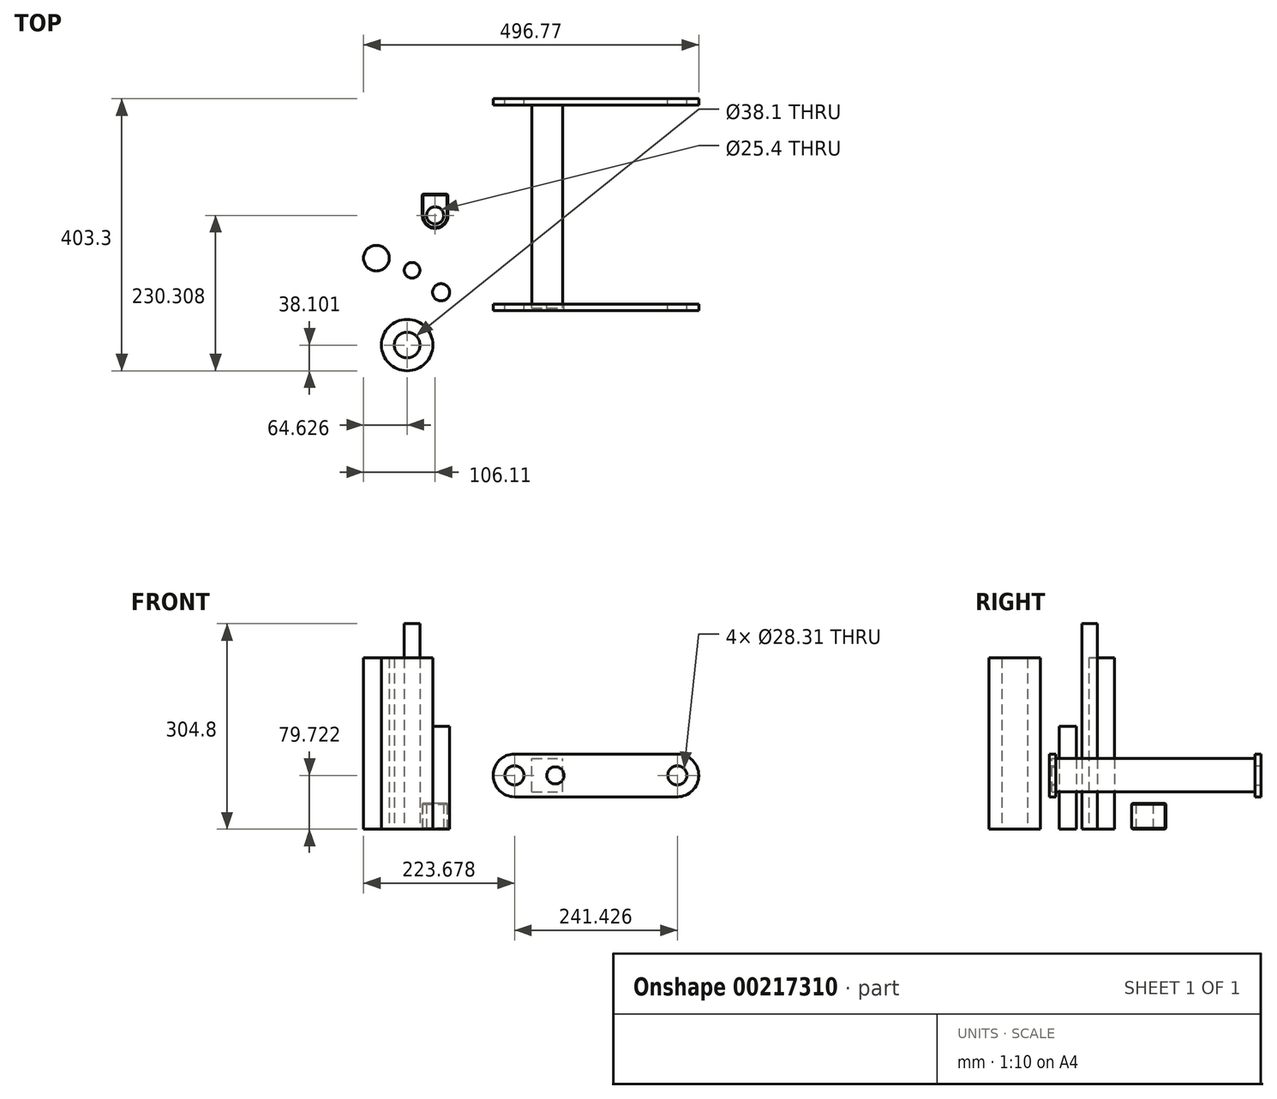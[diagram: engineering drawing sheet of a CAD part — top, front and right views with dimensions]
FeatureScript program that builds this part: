
annotation { "Feature Type Name" : "Feature", "Feature Type Description" : "" }
export const myFeature = defineFeature(function(context is Context, id is Id, definition is map)
    precondition{}
    {
        {
            var Q0;
            Q0=qCreatedBy(makeId("Front.planeOp"),FACE);
            var sketch = newSketch(context, id + "F0", { "sketchPlane" : qUnion([Q0])});
            skLineSegment(sketch, "E0.bottom", {"start": v(-15.65, 47.97) * mm, "end": v(225.65, 47.97) * mm});
            skLineSegment(sketch, "E0.top", {"start": v(-15.65, 111.47) * mm, "end": v(225.65, 111.47) * mm});
            skLineSegment(sketch, "E0.left", {"start": v(-47.4, 79.72) * mm, "end": v(-47.4, 79.72) * mm});
            skLineSegment(sketch, "E0.right", {"start": v(257.4, 79.72) * mm, "end": v(257.4, 79.72) * mm});
            skPoint(sketch, "E1.visualSharp", {"position": v(-47.4, 111.47) * mm});
            skArc(sketch, "E1.filletArc", {"start": v(-15.65, 111.47) * mm, "mid": v(-38.1, 102.17) * mm, "end": v(-47.4, 79.72) * mm});
            skPoint(sketch, "E2.visualSharp", {"position": v(-47.4, 47.97) * mm});
            skArc(sketch, "E2.filletArc", {"start": v(-47.4, 79.72) * mm, "mid": v(-38.1, 57.27) * mm, "end": v(-15.65, 47.97) * mm});
            skPoint(sketch, "E3.visualSharp", {"position": v(257.4, 47.97) * mm});
            skArc(sketch, "E3.filletArc", {"start": v(225.65, 47.97) * mm, "mid": v(248.1, 57.27) * mm, "end": v(257.4, 79.72) * mm});
            skPoint(sketch, "E4.visualSharp", {"position": v(257.4, 111.47) * mm});
            skArc(sketch, "E4.filletArc", {"start": v(257.4, 79.72) * mm, "mid": v(248.1, 102.17) * mm, "end": v(225.65, 111.47) * mm});
            skSolve(sketch);
        }
        {
            var Q0;
            Q0=makeQuery(id+"F0.imprint","IMPRINT",FACE,{"disambiguationData":[TD([[makeQuery(id+"F0.imprint","IMPRINT",EDGE,{"derivedFrom":sQuery(id+"F0.wireOp",EDGE,"E0.bottom")}),1.0]])]});
            var sketch = newSketch(context, id + "F1", { "sketchPlane" : qUnion([Q0])});
            skCircle(sketch, "E5", {"center": v(225.73, 79.72) * mm, "radius": 14.15 * mm});
            skCircle(sketch, "E6", {"center": v(-15.7, 79.72) * mm, "radius": 14.15 * mm});
            skSolve(sketch);
        }
        {
            var Q0;
            Q0=makeQuery(id+"F1.imprint","IMPRINT",FACE,{"disambiguationData":[TD([[makeQuery(id+"F1.imprint","IMPRINT",EDGE,{"derivedFrom":sQuery(id+"F1.wireOp",EDGE,"E5")}),-1.0]])]});
            var sketch = newSketch(context, id + "F2", { "sketchPlane" : qUnion([Q0])});
            skCircle(sketch, "E7", {"center": v(44.9, 79.72) * mm, "radius": 12.7 * mm});
            skSolve(sketch);
        }
        {
            var Q0;
            Q0=makeQuery(id+"F1.imprint","IMPRINT",FACE,{"disambiguationData":[TD([[makeQuery(id+"F1.imprint","IMPRINT",EDGE,{"derivedFrom":sQuery(id+"F1.wireOp",EDGE,"E5")}),-1.0]])]});
            var Q1;
            Q1 = qSketchRegion(id + "F2", true);
            extrude(context, id + "F3", {"entities" : qUnion([Q0, Q1]), "depth" : 9.52 * mm});
        }
        {
            var Q0;
            Q0=makeQuery(id+"F3.opExtrude","SWEPT_BODY",BODY,{"disambiguationData":[OSD([sQuery(id+"F0.wireOp",EDGE,"E0.bottom"),sQuery(id+"F0.wireOp",EDGE,"E0.top"),sQuery(id+"F0.wireOp",EDGE,"E1.filletArc"),sQuery(id+"F0.wireOp",EDGE,"E2.filletArc"),sQuery(id+"F0.wireOp",EDGE,"E3.filletArc"),sQuery(id+"F0.wireOp",EDGE,"E4.filletArc"),sQuery(id+"F1.wireOp",EDGE,"E5"),sQuery(id+"F1.wireOp",EDGE,"E6")])]});
            transform(context, id + "F4", {"entities" : qUnion([Q0]), "transformType" : TransformType.TRANSLATION_3D, "dx" : 0 * mm, "dy" : 304.8 * mm, "dz" : 0 * mm, "makeCopy" : true});
        }
        {
            var Q0;
            Q0=sQuery(id+"F1.wireOp",EDGE,"E6");
            extrude(context, id + "F5", {"bodyType" : ToolBodyType.SURFACE, "surfaceEntities" : qUnion([Q0]), "oppositeDirection" : true, "depth" : 335.28 * mm, "hasSecondDirection" : true, "secondDirectionOppositeDirection" : false, "secondDirectionDepth" : 48.26 * mm});
        }
        {
            var Q0;
            Q0=makeQuery(id+"F5.opExtrude","SWEPT_BODY",BODY,{"disambiguationData":[OSD([sQuery(id+"F1.wireOp",EDGE,"E6")])]});
            transform(context, id + "F6", {"entities" : qUnion([Q0]), "transformType" : TransformType.TRANSLATION_3D, "dx" : 241.3 * mm, "dy" : 0 * mm, "dz" : 0 * mm, "makeCopy" : true});
        }
        {
            var Q0;
            Q0=makeQuery(id+"F4.opPattern","COPY",FACE,{"derivedFrom":makeQuery(id+"F3.opExtrude","CAP_FACE",FACE,{"disambiguationData":[OSD([sQuery(id+"F0.wireOp",EDGE,"E0.bottom"),sQuery(id+"F0.wireOp",EDGE,"E0.top"),sQuery(id+"F0.wireOp",EDGE,"E1.filletArc"),sQuery(id+"F0.wireOp",EDGE,"E2.filletArc"),sQuery(id+"F0.wireOp",EDGE,"E3.filletArc"),sQuery(id+"F0.wireOp",EDGE,"E4.filletArc"),sQuery(id+"F1.wireOp",EDGE,"E5"),sQuery(id+"F1.wireOp",EDGE,"E6")])],"isStart":false}),"instanceName":"1"});
            var sketch = newSketch(context, id + "F7", { "sketchPlane" : qUnion([Q0])});
            skLineSegment(sketch, "E8.bottom", {"start": v(10.28, 55.34) * mm, "end": v(56, 55.34) * mm});
            skLineSegment(sketch, "E8.top", {"start": v(10.28, 104.82) * mm, "end": v(56, 104.82) * mm});
            skLineSegment(sketch, "E8.left", {"start": v(10.28, 55.34) * mm, "end": v(10.28, 104.82) * mm});
            skLineSegment(sketch, "E8.right", {"start": v(56, 55.34) * mm, "end": v(56, 104.82) * mm});
            skSolve(sketch);
        }
        {
            var Q0;
            Q0=makeQuery(id+"F7.imprint","IMPRINT",FACE,{"disambiguationData":[TD([[makeQuery(id+"F7.imprint","IMPRINT",EDGE,{"derivedFrom":sQuery(id+"F7.wireOp",EDGE,"E8.bottom")}),1.0]])]});
            extrude(context, id + "F8", {"entities" : qUnion([Q0]), "depth" : 301 * mm});
        }
        {
            var Q0;
            Q0=qCreatedBy(makeId("Top.planeOp"),FACE);
            var sketch = newSketch(context, id + "F9", { "sketchPlane" : qUnion([Q0])});
            skCircle(sketch, "E9", {"center": v(-167.47, 50.47) * mm, "radius": 11.62 * mm});
            skSolve(sketch);
        }
        {
            var Q0;
            Q0=makeQuery(id+"F9.imprint","IMPRINT",FACE,{"disambiguationData":[TD([[makeQuery(id+"F9.imprint","IMPRINT",EDGE,{"derivedFrom":sQuery(id+"F9.wireOp",EDGE,"E9")}),1.0]])]});
            extrude(context, id + "F10", {"entities" : qUnion([Q0]), "depth" : 304.8 * mm});
        }
        {
            var Q0;
            Q0=qCreatedBy(makeId("Top.planeOp"),FACE);
            var sketch = newSketch(context, id + "F11", { "sketchPlane" : qUnion([Q0])});
            skCircle(sketch, "E10", {"center": v(-174.74, -60.4) * mm, "radius": 38.1 * mm});
            skCircle(sketch, "E11", {"center": v(-222.28, 28.18) * mm, "radius": 13.92 * mm});
            skCircle(sketch, "E12", {"center": v(-220.32, 68.55) * mm, "radius": 19.05 * mm});
            skCircle(sketch, "E13.0", {"center": v(-174.74, -60.4) * mm, "radius": 19.05 * mm});
            skSolve(sketch);
        }
        {
            var Q0;
            Q0=makeQuery(id+"F11.imprint","IMPRINT",FACE,{"disambiguationData":[TD([[makeQuery(id+"F11.imprint","IMPRINT",EDGE,{"derivedFrom":sQuery(id+"F11.wireOp",EDGE,"E10")}),1.0]])]});
            extrude(context, id + "F12", {"entities" : qUnion([Q0]), "depth" : 254 * mm});
        }
        {
            var Q0;
            Q0=makeQuery(id+"F11.imprint","IMPRINT",FACE,{"disambiguationData":[TD([[makeQuery(id+"F11.imprint","IMPRINT",EDGE,{"derivedFrom":sQuery(id+"F11.wireOp",EDGE,"E12")}),1.0]])]});
            extrude(context, id + "F13", {"entities" : qUnion([Q0]), "depth" : 254 * mm});
        }
        {
            var Q0;
            Q0=qCreatedBy(makeId("Top.planeOp"),FACE);
            var sketch = newSketch(context, id + "F14", { "sketchPlane" : qUnion([Q0])});
            skLineSegment(sketch, "E14.bottom", {"start": v(-152.3, 163.56) * mm, "end": v(-114.2, 163.56) * mm});
            skLineSegment(sketch, "E14.top", {"start": v(-133.26, 112.76) * mm, "end": v(-133.26, 112.76) * mm});
            skLineSegment(sketch, "E14.left", {"start": v(-152.3, 163.56) * mm, "end": v(-152.3, 131.8) * mm});
            skLineSegment(sketch, "E14.right", {"start": v(-114.2, 163.56) * mm, "end": v(-114.2, 131.8) * mm});
            skPoint(sketch, "E15.visualSharp", {"position": v(-114.2, 112.76) * mm});
            skArc(sketch, "E15.filletArc", {"start": v(-133.26, 112.76) * mm, "mid": v(-119.79, 118.34) * mm, "end": v(-114.2, 131.8) * mm});
            skPoint(sketch, "E16.visualSharp", {"position": v(-152.3, 112.76) * mm});
            skArc(sketch, "E16.filletArc", {"start": v(-152.3, 131.8) * mm, "mid": v(-146.73, 118.34) * mm, "end": v(-133.26, 112.76) * mm});
            skCircle(sketch, "E17", {"center": v(-133.26, 131.8) * mm, "radius": 12.7 * mm});
            skSolve(sketch);
        }
        {
            var Q0;
            Q0=makeQuery(id+"F14.imprint","IMPRINT",FACE,{"disambiguationData":[TD([[makeQuery(id+"F14.imprint","IMPRINT",EDGE,{"derivedFrom":sQuery(id+"F14.wireOp",EDGE,"E14.bottom")}),-1.0]])]});
            extrude(context, id + "F15", {"entities" : qUnion([Q0]), "depth" : 38.1 * mm});
        }
        {
            var Q0;
            Q0=makeQuery(id+"F15.opExtrude","CAP_EDGE",EDGE,{"disambiguationData":[OSD([sQuery(id+"F14.wireOp",EDGE,"E14.right")])],"isStart":true});
            var Q1;
            Q1=makeQuery(id+"F15.opExtrude","CAP_EDGE",EDGE,{"disambiguationData":[OSD([sQuery(id+"F14.wireOp",EDGE,"E15.filletArc"),sQuery(id+"F14.wireOp",EDGE,"E16.filletArc")])],"isStart":true});
            var Q2;
            Q2=makeQuery(id+"F15.opExtrude","CAP_EDGE",EDGE,{"disambiguationData":[OSD([sQuery(id+"F14.wireOp",EDGE,"E14.left")])],"isStart":true});
            var Q3;
            Q3=makeQuery(id+"F15.opExtrude","CAP_EDGE",EDGE,{"disambiguationData":[OSD([sQuery(id+"F14.wireOp",EDGE,"E14.bottom")])],"isStart":true});
            var Q4;
            Q4=makeQuery(id+"F15.opExtrude","SWEPT_EDGE",EDGE,{"disambiguationData":[OSD([sQuery(id+"F14.wireOp",EDGE,"E14.bottom"),sQuery(id+"F14.wireOp",EDGE,"E14.right")])]});
            var Q5;
            Q5=makeQuery(id+"F15.opExtrude","SWEPT_EDGE",EDGE,{"disambiguationData":[OSD([sQuery(id+"F14.wireOp",EDGE,"E14.bottom"),sQuery(id+"F14.wireOp",EDGE,"E14.left")])]});
            var Q6;
            Q6=makeQuery(id+"F15.opExtrude","CAP_EDGE",EDGE,{"disambiguationData":[OSD([sQuery(id+"F14.wireOp",EDGE,"E14.bottom")])],"isStart":false});
            var Q7;
            Q7=makeQuery(id+"F15.opExtrude","CAP_EDGE",EDGE,{"disambiguationData":[OSD([sQuery(id+"F14.wireOp",EDGE,"E14.left")])],"isStart":false});
            var Q8;
            Q8=makeQuery(id+"F15.opExtrude","CAP_EDGE",EDGE,{"disambiguationData":[OSD([sQuery(id+"F14.wireOp",EDGE,"E14.right")])],"isStart":false});
            var Q9;
            Q9=makeQuery(id+"F15.opExtrude","CAP_EDGE",EDGE,{"disambiguationData":[OSD([sQuery(id+"F14.wireOp",EDGE,"E15.filletArc"),sQuery(id+"F14.wireOp",EDGE,"E16.filletArc")])],"isStart":false});
            chamfer(context, id + "F16", {"entities" : qUnion([Q0, Q1, Q2, Q3, Q4, Q5, Q6, Q7, Q8, Q9]), "width" : 1.27 * mm, "tangentPropagation" : true});
        }
        {
            var Q0;
            Q0=qCreatedBy(makeId("Top.planeOp"),FACE);
            var sketch = newSketch(context, id + "F17", { "sketchPlane" : qUnion([Q0])});
            skCircle(sketch, "E18", {"center": v(-124.55, 17.82) * mm, "radius": 12.7 * mm});
            skSolve(sketch);
        }
        {
            var Q0;
            Q0=makeQuery(id+"F17.imprint","IMPRINT",FACE,{"disambiguationData":[TD([[makeQuery(id+"F17.imprint","IMPRINT",EDGE,{"derivedFrom":sQuery(id+"F17.wireOp",EDGE,"E18")}),1.0]])]});
            extrude(context, id + "F18", {"entities" : qUnion([Q0]), "depth" : 152.4 * mm});
        }
        {
            var Q0;
            Q0=qCreatedBy(makeId("Top.planeOp"),FACE);
            var sketch = newSketch(context, id + "F19", { "sketchPlane" : qUnion([Q0])});
            skLineSegment(sketch, "E19.bottom", {"start": v(-875.07, 0) * mm, "end": v(-748.07, 0) * mm});
            skLineSegment(sketch, "E19.top", {"start": v(-875.07, -50.8) * mm, "end": v(-748.07, -50.8) * mm});
            skLineSegment(sketch, "E19.left", {"start": v(-875.07, 0) * mm, "end": v(-875.07, -50.8) * mm});
            skLineSegment(sketch, "E19.right", {"start": v(-748.07, 0) * mm, "end": v(-748.07, -50.8) * mm});
            skLineSegment(sketch, "E20", {"start": v(-875.07, -6.14) * mm, "end": v(-834.6, -6.14) * mm});
            skLineSegment(sketch, "E21", {"start": v(-834.6, -6.14) * mm, "end": v(-808.02, -50.8) * mm});
            skLineSegment(sketch, "E22", {"start": v(-808.02, -50.8) * mm, "end": v(-775.08, -50.8) * mm});
            skLineSegment(sketch, "E23", {"start": v(-775.08, -50.8) * mm, "end": v(-748.07, -6.14) * mm});
            skLineSegment(sketch, "E24.0", {"start": v(-771.5, -57.15) * mm, "end": v(-742.64, -9.42) * mm});
            skLineSegment(sketch, "E24.1", {"start": v(-811.63, -57.15) * mm, "end": v(-771.5, -57.15) * mm});
            skLineSegment(sketch, "E24.2", {"start": v(-838.2, -12.49) * mm, "end": v(-811.63, -57.15) * mm});
            skLineSegment(sketch, "E24.3", {"start": v(-875.07, -12.49) * mm, "end": v(-838.2, -12.49) * mm});
            skSolve(sketch);
        }
    });
